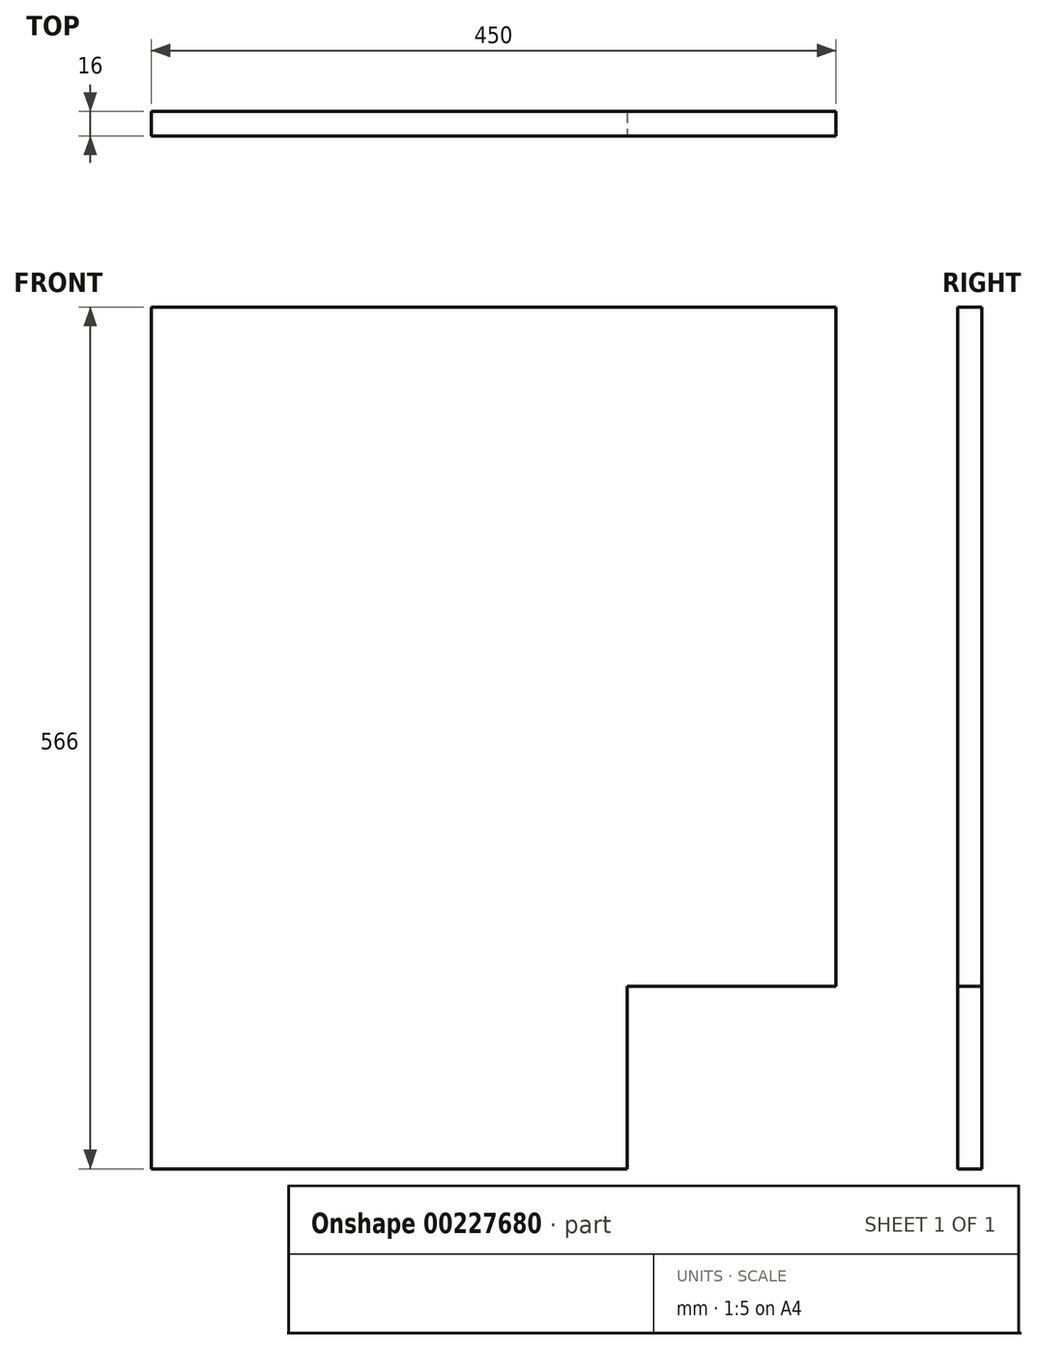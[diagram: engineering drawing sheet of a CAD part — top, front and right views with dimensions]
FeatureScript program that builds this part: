
annotation { "Feature Type Name" : "Feature", "Feature Type Description" : "" }
export const myFeature = defineFeature(function(context is Context, id is Id, definition is map)
    precondition{}
    {
        {
            var Q0;
            Q0=qCreatedBy(makeId("Front.planeOp"),FACE);
            var sketch = newSketch(context, id + "F0", { "sketchPlane" : qUnion([Q0])});
            skLineSegment(sketch, "E0.bottom", {"start": v(225, -283) * mm, "end": v(-225, -283) * mm});
            skLineSegment(sketch, "E0.top", {"start": v(225, 283) * mm, "end": v(-225, 283) * mm});
            skLineSegment(sketch, "E0.left", {"start": v(225, -283) * mm, "end": v(225, 283) * mm});
            skLineSegment(sketch, "E0.right", {"start": v(-225, -283) * mm, "end": v(-225, 283) * mm});
            skPoint(sketch, "E0.middle", {"position": v(0, 0) * mm});
            skSolve(sketch);
        }
        {
            var Q0;
            Q0 = qSketchRegion(id + "F0", true);
            extrude(context, id + "F1", {"entities" : qUnion([Q0]), "depth" : 16 * mm, "symmetric" : true});
        }
        {
            var Q0;
            Q0=makeQuery(id+"F1.opExtrude","CAP_FACE",FACE,{"disambiguationData":[OSD([sQuery(id+"F0.wireOp",EDGE,"E0.bottom"),sQuery(id+"F0.wireOp",EDGE,"E0.top"),sQuery(id+"F0.wireOp",EDGE,"E0.left"),sQuery(id+"F0.wireOp",EDGE,"E0.right")])],"isStart":false});
            var sketch = newSketch(context, id + "F2", { "sketchPlane" : qUnion([Q0])});
            skLineSegment(sketch, "E1.bottom", {"start": v(225, -283) * mm, "end": v(88, -283) * mm});
            skLineSegment(sketch, "E1.top", {"start": v(225, -163) * mm, "end": v(88, -163) * mm});
            skLineSegment(sketch, "E1.left", {"start": v(225, -283) * mm, "end": v(225, -163) * mm});
            skLineSegment(sketch, "E1.right", {"start": v(88, -283) * mm, "end": v(88, -163) * mm});
            skSolve(sketch);
        }
        {
            var Q0;
            Q0 = qSketchRegion(id + "F2", true);
            extrude(context, id + "F3", {"entities" : qUnion([Q0]), "operationType" : NewBodyOperationType.REMOVE, "endBound" : BoundingType.THROUGH_ALL, "oppositeDirection" : true, "depth" : 25 * mm});
        }
    });
